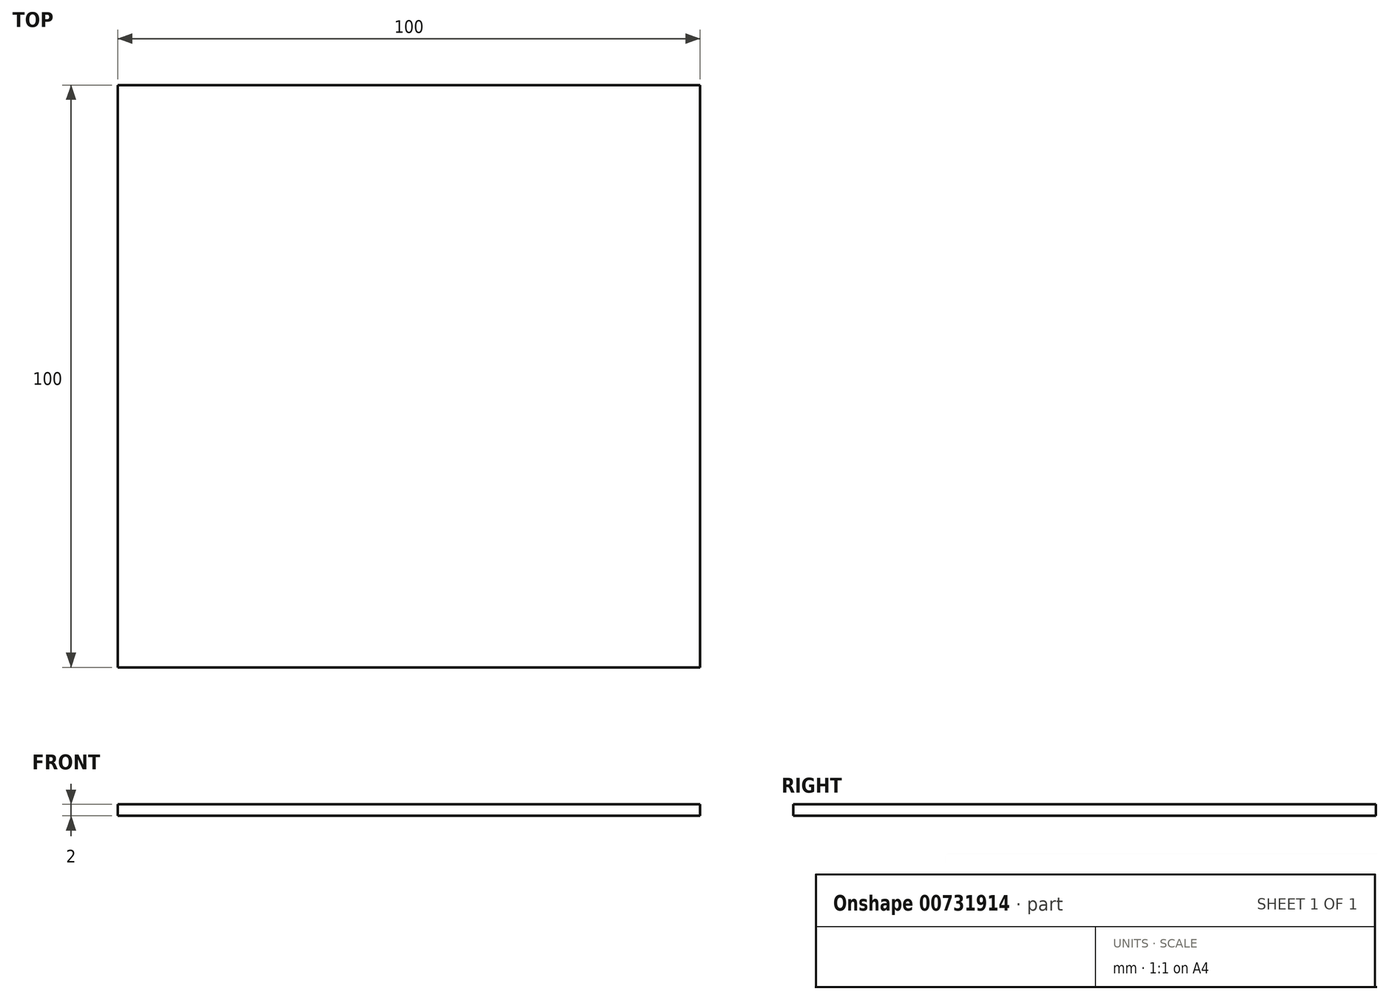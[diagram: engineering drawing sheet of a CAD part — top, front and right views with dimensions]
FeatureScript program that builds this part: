
annotation { "Feature Type Name" : "Feature", "Feature Type Description" : "" }
export const myFeature = defineFeature(function(context is Context, id is Id, definition is map)
    precondition{}
    {
        {
            var Q0;
            Q0=qCreatedBy(makeId("Top.planeOp"),FACE);
            var sketch = newSketch(context, id + "F0", { "sketchPlane" : qUnion([Q0])});
            skLineSegment(sketch, "E0.bottom", {"start": v(50, -50) * mm, "end": v(-50, -50) * mm});
            skLineSegment(sketch, "E0.top", {"start": v(50, 50) * mm, "end": v(-50, 50) * mm});
            skLineSegment(sketch, "E0.left", {"start": v(50, -50) * mm, "end": v(50, 50) * mm});
            skLineSegment(sketch, "E0.right", {"start": v(-50, -50) * mm, "end": v(-50, 50) * mm});
            skPoint(sketch, "E0.middle", {"position": v(0, 0) * mm});
            skSolve(sketch);
        }
        {
            var Q0;
            Q0=qSketchRegion(id+"F0",true);
            extrude(context, id + "F1", {"entities" : qUnion([Q0]), "depth" : 2 * mm, "offsetDistance" : 25 * mm});
        }
    });
